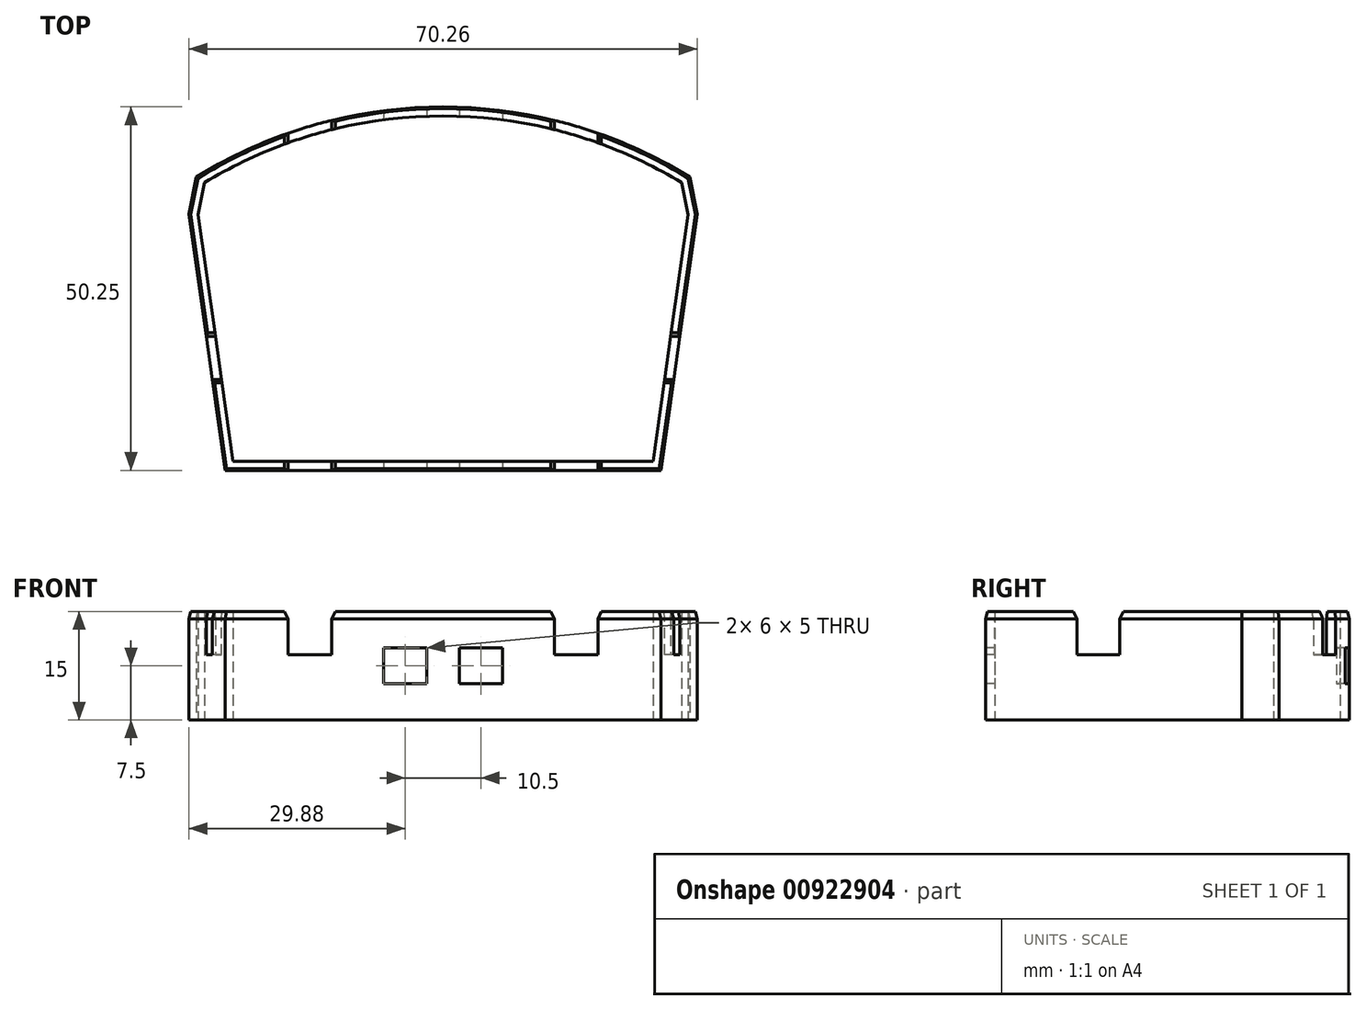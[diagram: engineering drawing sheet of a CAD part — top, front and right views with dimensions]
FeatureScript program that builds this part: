
annotation { "Feature Type Name" : "Feature", "Feature Type Description" : "" }
export const myFeature = defineFeature(function(context is Context, id is Id, definition is map)
    precondition{}
    {
        {
            var Q0;
            Q0=qCreatedBy(makeId("Top.planeOp"),FACE);
            var sketch = newSketch(context, id + "F0", { "sketchPlane" : qUnion([Q0])});
            skLineSegment(sketch, "E0", {"start": v(-30.12, 0) * mm, "end": v(30.12, 0) * mm});
            skLineSegment(sketch, "E1", {"start": v(-30.13, 0) * mm, "end": v(-35.13, 35.4) * mm});
            skLineSegment(sketch, "E2", {"start": v(-35.13, 35.4) * mm, "end": v(-34.13, 40.55) * mm});
            skArc(sketch, "E3", {"start": v(34.12, 40.55) * mm, "mid": v(0, 50.25) * mm, "end": v(-34.12, 40.55) * mm});
            skLineSegment(sketch, "E4", {"start": v(0, 50.25) * mm, "end": v(0, 0) * mm});
            skLineSegment(sketch, "E5.MirrorCS", {"start": v(30.12, 0) * mm, "end": v(35.12, 35.4) * mm});
            skLineSegment(sketch, "E6.MirrorCS", {"start": v(35.13, 35.4) * mm, "end": v(34.13, 40.55) * mm});
            skLineSegment(sketch, "E7.0", {"start": v(33.86, 35.37) * mm, "end": v(33, 39.77) * mm});
            skLineSegment(sketch, "E7.1", {"start": v(-33.86, 35.37) * mm, "end": v(-33, 39.77) * mm});
            skLineSegment(sketch, "E7.2", {"start": v(-29.04, 1.25) * mm, "end": v(-33.86, 35.37) * mm});
            skArc(sketch, "E7.3", {"start": v(33, 39.77) * mm, "mid": v(0, 49) * mm, "end": v(-33, 39.77) * mm});
            skLineSegment(sketch, "E7.4", {"start": v(-29.04, 1.25) * mm, "end": v(29.04, 1.25) * mm});
            skLineSegment(sketch, "E7.5", {"start": v(29.04, 1.25) * mm, "end": v(33.86, 35.37) * mm});
            skSolve(sketch);
        }
        {
            var Q0;
            {var subQ1=sQuery(id+"F0.wireOp",EDGE,"E1");Q0=makeQuery(id+"F0.imprint","IMPRINT",FACE,{"disambiguationData":[TD([[makeQuery(id+"F0.imprint","IMPRINT",EDGE,{"derivedFrom":subQ1}),-1.0]])]});}
            var Q1;
            {var subQ11=sQuery(id+"F0.wireOp",EDGE,"E5.MirrorCS");Q1=makeQuery(id+"F0.imprint","IMPRINT",FACE,{"disambiguationData":[TD([[makeQuery(id+"F0.imprint","IMPRINT",EDGE,{"derivedFrom":subQ11}),1.0]])]});}
            extrude(context, id + "F1", {"entities" : qUnion([Q0, Q1]), "depth" : 12 * mm, "offsetDistance" : 25 * mm});
        }
        {
            var Q0;
            Q0=makeQuery(id+"F1.opExtrude","CAP_EDGE",EDGE,{"disambiguationData":[OSD([sQuery(id+"F0.wireOp",EDGE,"E1")])],"isStart":false});
            var Q1;
            Q1=makeQuery(id+"F1.opExtrude","CAP_EDGE",EDGE,{"disambiguationData":[OSD([sQuery(id+"F0.wireOp",EDGE,"E0")])],"isStart":false});
            var Q2;
            Q2=makeQuery(id+"F1.opExtrude","CAP_EDGE",EDGE,{"disambiguationData":[OSD([sQuery(id+"F0.wireOp",EDGE,"E5.MirrorCS")])],"isStart":false});
            var Q3;
            Q3=makeQuery(id+"F1.opExtrude","CAP_EDGE",EDGE,{"disambiguationData":[OSD([sQuery(id+"F0.wireOp",EDGE,"E3")])],"isStart":false});
            var Q4;
            Q4=makeQuery(id+"F1.opExtrude","CAP_EDGE",EDGE,{"disambiguationData":[OSD([sQuery(id+"F0.wireOp",EDGE,"E6.MirrorCS")])],"isStart":false});
            var Q5;
            Q5=makeQuery(id+"F1.opExtrude","CAP_EDGE",EDGE,{"disambiguationData":[OSD([sQuery(id+"F0.wireOp",EDGE,"E2")])],"isStart":false});
            chamfer(context, id + "F2", {"entities" : qUnion([Q0, Q1, Q2, Q3, Q4, Q5]), "chamferType" : ChamferType.TWO_OFFSETS, "width1" : .25 * mm, "oppositeDirection" : true, "width2" : 1 * mm, "tangentPropagation" : true});
        }
        {
            var Q0;
            Q0=makeQuery(id+"F1.opExtrude","SWEPT_FACE",FACE,{"disambiguationData":[OSD([sQuery(id+"F0.wireOp",EDGE,"E0")])]});
            var sketch = newSketch(context, id + "F3", { "sketchPlane" : qUnion([Q0])});
            skLineSegment(sketch, "E8", {"start": v(-8.25, 2) * mm, "end": v(-2.25, 2) * mm});
            skLineSegment(sketch, "E9", {"start": v(-8.25, 2) * mm, "end": v(-8.25, 7) * mm});
            skLineSegment(sketch, "E10", {"start": v(-2.25, 2) * mm, "end": v(-2.25, 7) * mm});
            skLineSegment(sketch, "E11", {"start": v(-8.25, 7) * mm, "end": v(-2.25, 7) * mm});
            skLineSegment(sketch, "E12.MirrorCS", {"start": v(2.25, 2) * mm, "end": v(2.25, 7) * mm});
            skLineSegment(sketch, "E13.MirrorCS", {"start": v(8.25, 7) * mm, "end": v(2.25, 7) * mm});
            skLineSegment(sketch, "E14.MirrorCS", {"start": v(8.25, 2) * mm, "end": v(8.25, 7) * mm});
            skLineSegment(sketch, "E15.MirrorCS", {"start": v(8.25, 2) * mm, "end": v(2.25, 2) * mm});
            skLineSegment(sketch, "E16.0", {"start": v(-29.9, 12) * mm, "end": v(29.9, 12) * mm, "construction": true});
            skLineSegment(sketch, "E17.0", {"start": v(30.12, 11) * mm, "end": v(-30.12, 11) * mm, "construction": true});
            skLineSegment(sketch, "E18", {"start": v(-21.4, 11) * mm, "end": v(-21.4, 6) * mm});
            skLineSegment(sketch, "E19", {"start": v(-21.4, 6) * mm, "end": v(-15.4, 6) * mm});
            skLineSegment(sketch, "E20", {"start": v(-15.4, 6) * mm, "end": v(-15.4, 11) * mm});
            skLineSegment(sketch, "E21", {"start": v(-21.4, 11) * mm, "end": v(-21.9, 12) * mm});
            skLineSegment(sketch, "E22", {"start": v(-15.4, 11) * mm, "end": v(-14.9, 12) * mm});
            skLineSegment(sketch, "E23", {"start": v(-18.4, 6) * mm, "end": v(-18.4, 12) * mm, "construction": true});
            skLineSegment(sketch, "E24", {"start": v(-21.9, 12) * mm, "end": v(-14.9, 12) * mm});
            skPoint(sketch, "E25", {"position": v(-18.4, 12) * mm});
            skLineSegment(sketch, "E26", {"start": v(-21.4, 11) * mm, "end": v(-15.4, 11) * mm, "construction": true});
            skPoint(sketch, "E27", {"position": v(-18.4, 11) * mm});
            skLineSegment(sketch, "E28.MirrorCS", {"start": v(21.4, 6) * mm, "end": v(15.4, 6) * mm});
            skLineSegment(sketch, "E29.MirrorCS", {"start": v(21.4, 11) * mm, "end": v(21.4, 6) * mm});
            skLineSegment(sketch, "E30.MirrorCS", {"start": v(21.4, 11) * mm, "end": v(21.9, 12) * mm});
            skLineSegment(sketch, "E31.MirrorCS", {"start": v(21.9, 12) * mm, "end": v(14.9, 12) * mm});
            skLineSegment(sketch, "E32.MirrorCS", {"start": v(15.4, 11) * mm, "end": v(14.9, 12) * mm});
            skLineSegment(sketch, "E33.MirrorCS", {"start": v(15.4, 6) * mm, "end": v(15.4, 11) * mm});
            skSolve(sketch);
        }
        {
            var Q0;
            {var subQ0=sQuery(id+"F3.wireOp",EDGE,"E18");Q0=makeQuery(id+"F3.imprint","IMPRINT",FACE,{"disambiguationData":[TD([[makeQuery(id+"F3.imprint","IMPRINT",EDGE,{"derivedFrom":subQ0}),1.0]])]});}
            var Q1;
            {var subQ0=sQuery(id+"F3.wireOp",EDGE,"E21");Q1=makeQuery(id+"F3.imprint","IMPRINT",FACE,{"disambiguationData":[TD([[makeQuery(id+"F3.imprint","IMPRINT",EDGE,{"derivedFrom":subQ0}),-1.0]])]});}
            var Q2;
            Q2=makeQuery(id+"F3.imprint","IMPRINT",FACE,{"disambiguationData":[TD([[makeQuery(id+"F3.imprint","IMPRINT",EDGE,{"derivedFrom":sQuery(id+"F3.wireOp",EDGE,"E28.MirrorCS")}),-1.0]])]});
            var Q3;
            {var subQ0=sQuery(id+"F3.wireOp",EDGE,"E30.MirrorCS");Q3=makeQuery(id+"F3.imprint","IMPRINT",FACE,{"disambiguationData":[TD([[makeQuery(id+"F3.imprint","IMPRINT",EDGE,{"derivedFrom":subQ0}),1.0]])]});}
            var Q4;
            Q4=makeQuery(id+"F3.imprint","IMPRINT",FACE,{"disambiguationData":[TD([[makeQuery(id+"F3.imprint","IMPRINT",EDGE,{"derivedFrom":sQuery(id+"F3.wireOp",EDGE,"E8")}),1.0]])]});
            var Q5;
            Q5=makeQuery(id+"F3.imprint","IMPRINT",FACE,{"disambiguationData":[TD([[makeQuery(id+"F3.imprint","IMPRINT",EDGE,{"derivedFrom":sQuery(id+"F3.wireOp",EDGE,"E12.MirrorCS")}),-1.0]])]});
            extrude(context, id + "F4", {"entities" : qUnion([Q0, Q1, Q2, Q3, Q4, Q5]), "operationType" : NewBodyOperationType.REMOVE, "endBound" : BoundingType.THROUGH_ALL, "oppositeDirection" : true, "depth" : 25 * mm, "offsetDistance" : 25 * mm});
        }
        {
            var Q0;
            Q0=makeQuery(id+"F1.opExtrude","SWEPT_EDGE",EDGE,{"disambiguationData":[OSD([sQuery(id+"F0.wireOp",EDGE,"E1"),sQuery(id+"F0.wireOp",EDGE,"E2")])]});
            cPlane(context, id + "F5", {"entities" : qUnion([Q0]), "cplaneType" : CPlaneType.LINE_ANGLE, "offset" : 25 * mm, "angle" : 0 * degree, "width" : 150 * mm, "height" : 150 * mm});
        }
        {
            var Q0;
            Q0=makeQuery(id+"F1.opExtrude","SWEPT_FACE",FACE,{"disambiguationData":[OSD([sQuery(id+"F0.wireOp",EDGE,"E1")])]});
            var sketch = newSketch(context, id + "F6", { "sketchPlane" : qUnion([Q0])});
            skLineSegment(sketch, "E34.0.0", {"start": v(-4.21, 0) * mm, "end": v(-4.21, 11) * mm});
            skLineSegment(sketch, "E34.0.1", {"start": v(-4.21, 11) * mm, "end": v(-39.96, 11) * mm});
            skLineSegment(sketch, "E34.0.2", {"start": v(-39.96, 11) * mm, "end": v(-39.96, 0) * mm});
            skLineSegment(sketch, "E34.0.3", {"start": v(-39.96, 0) * mm, "end": v(-4.21, 0) * mm});
            skLineSegment(sketch, "E35.0", {"start": v(-39.92, 12) * mm, "end": v(-4.43, 12) * mm});
            skLineSegment(sketch, "E36", {"start": v(-22.93, 11) * mm, "end": v(-22.93, 6) * mm});
            skLineSegment(sketch, "E37", {"start": v(-22.93, 6) * mm, "end": v(-16.93, 6) * mm});
            skLineSegment(sketch, "E38", {"start": v(-16.93, 6) * mm, "end": v(-16.93, 11) * mm});
            skLineSegment(sketch, "E39", {"start": v(-22.93, 11) * mm, "end": v(-23.43, 12) * mm});
            skLineSegment(sketch, "E40", {"start": v(-16.93, 11) * mm, "end": v(-16.43, 12) * mm});
            skLineSegment(sketch, "E41", {"start": v(-19.93, 6) * mm, "end": v(-19.93, 12) * mm, "construction": true});
            skLineSegment(sketch, "E42", {"start": v(-23.43, 12) * mm, "end": v(-16.43, 12) * mm});
            skPoint(sketch, "E43", {"position": v(-19.93, 12) * mm});
            skLineSegment(sketch, "E44", {"start": v(-22.93, 11) * mm, "end": v(-16.93, 11) * mm, "construction": true});
            skPoint(sketch, "E45", {"position": v(-19.93, 11) * mm});
            skSolve(sketch);
        }
        {
            var Q0;
            Q0=qCreatedBy(id+"F5.planeOp",FACE);
            var sketch = newSketch(context, id + "F7", { "sketchPlane" : qUnion([Q0])});
            skLineSegment(sketch, "E46.0", {"start": v(-18.53, 11) * mm, "end": v(-18.53, 6) * mm});
            skLineSegment(sketch, "E47.0", {"start": v(-18.53, 11) * mm, "end": v(-19.03, 12) * mm});
            skLineSegment(sketch, "E48.0", {"start": v(-19.03, 12) * mm, "end": v(-12.1, 12) * mm});
            skLineSegment(sketch, "E49.0", {"start": v(-12.6, 11) * mm, "end": v(-12.1, 12) * mm});
            skLineSegment(sketch, "E50.0", {"start": v(-12.6, 6) * mm, "end": v(-12.6, 11) * mm});
            skLineSegment(sketch, "E51.0", {"start": v(-18.53, 6) * mm, "end": v(-12.6, 6) * mm});
            skSolve(sketch);
        }
        {
            var Q0;
            Q0=makeQuery(id+"F7.imprint","IMPRINT",FACE,{"disambiguationData":[TD([[makeQuery(id+"F7.imprint","IMPRINT",EDGE,{"derivedFrom":sQuery(id+"F7.wireOp",EDGE,"E46.0")}),1.0]])]});
            extrude(context, id + "F8", {"entities" : qUnion([Q0]), "operationType" : NewBodyOperationType.REMOVE, "endBound" : BoundingType.THROUGH_ALL, "oppositeDirection" : true, "depth" : 25 * mm, "offsetDistance" : 25 * mm});
        }
        {
            var Q0;
            {var subQ0=sQuery(id+"F0.wireOp",EDGE,"E2");var subQ1=sQuery(id+"F0.wireOp",EDGE,"E1");var subQ2=sQuery(id+"F0.wireOp",EDGE,"E3");var subQ3=sQuery(id+"F0.wireOp",EDGE,"E0");var subQ4=sQuery(id+"F0.wireOp",EDGE,"E7.3");var subQ5=sQuery(id+"F0.wireOp",EDGE,"E7.1");var subQ6=sQuery(id+"F0.wireOp",EDGE,"E7.2");var subQ7=sQuery(id+"F0.wireOp",EDGE,"E7.4");Q0=makeQuery(id+"F4.boolean.opBoolean","SPLIT",FACE,{"disambiguationData":[TD([makeQuery(id+"F1.opExtrude","SWEPT_FACE",FACE,{"disambiguationData":[OSD([subQ3])]}),makeQuery(id+"F1.opExtrude","SWEPT_FACE",FACE,{"disambiguationData":[OSD([subQ1])]}),makeQuery(id+"F1.opExtrude","SWEPT_FACE",FACE,{"disambiguationData":[OSD([subQ0])]}),makeQuery(id+"F1.opExtrude","SWEPT_FACE",FACE,{"disambiguationData":[OSD([subQ2])]}),makeQuery(id+"F1.opExtrude","SWEPT_FACE",FACE,{"disambiguationData":[OSD([subQ5])]}),makeQuery(id+"F1.opExtrude","SWEPT_FACE",FACE,{"disambiguationData":[OSD([subQ6])]}),makeQuery(id+"F1.opExtrude","SWEPT_FACE",FACE,{"disambiguationData":[OSD([subQ4])]}),makeQuery(id+"F1.opExtrude","SWEPT_FACE",FACE,{"disambiguationData":[OSD([subQ7])]}),makeQuery(id+"F4.opExtrude","SWEPT_FACE",FACE,{"disambiguationData":[OSD([sQuery(id+"F3.wireOp",EDGE,"E9")])]})])],"derivedFrom":makeQuery(id+"F1.opExtrude","CAP_FACE",FACE,{"disambiguationData":[OSD([subQ3,subQ1,subQ0,subQ2,sQuery(id+"F0.wireOp",EDGE,"E5.MirrorCS"),sQuery(id+"F0.wireOp",EDGE,"E6.MirrorCS"),sQuery(id+"F0.wireOp",EDGE,"E7.0"),subQ5,subQ6,subQ4,subQ7,sQuery(id+"F0.wireOp",EDGE,"E7.5")])],"isStart":true})});}
            var sketch = newSketch(context, id + "F9", { "sketchPlane" : qUnion([Q0])});
            skLineSegment(sketch, "E52.0", {"start": v(-30.12, 0) * mm, "end": v(30.12, 0) * mm});
            skLineSegment(sketch, "E53.0", {"start": v(-35.13, -35.4) * mm, "end": v(-30.13, 0) * mm});
            skLineSegment(sketch, "E54.0", {"start": v(-35.13, -35.4) * mm, "end": v(-34.13, -40.55) * mm});
            skArc(sketch, "E55.0", {"start": v(34.12, -40.55) * mm, "mid": v(0, -50.25) * mm, "end": v(-34.12, -40.55) * mm});
            skLineSegment(sketch, "E56.0", {"start": v(35.13, -35.4) * mm, "end": v(34.13, -40.55) * mm});
            skLineSegment(sketch, "E57.0", {"start": v(30.12, 0) * mm, "end": v(35.12, -35.4) * mm});
            skLineSegment(sketch, "E58.0", {"start": v(-29.04, -1.25) * mm, "end": v(29.04, -1.25) * mm});
            skLineSegment(sketch, "E59.0", {"start": v(-29.04, -1.25) * mm, "end": v(-33.86, -35.37) * mm});
            skLineSegment(sketch, "E60.0", {"start": v(-33.86, -35.37) * mm, "end": v(-33, -39.77) * mm});
            skArc(sketch, "E61.0", {"start": v(33, -39.77) * mm, "mid": v(0, -49) * mm, "end": v(-33, -39.77) * mm});
            skLineSegment(sketch, "E62.0", {"start": v(33.86, -35.37) * mm, "end": v(33, -39.77) * mm});
            skLineSegment(sketch, "E63.0", {"start": v(29.04, -1.25) * mm, "end": v(33.86, -35.37) * mm});
            skSolve(sketch);
        }
        {
            var Q0;
            {var subQ1=sQuery(id+"F9.wireOp",EDGE,"E53.0");Q0=makeQuery(id+"F9.imprint","IMPRINT",FACE,{"disambiguationData":[TD([[makeQuery(id+"F9.imprint","IMPRINT",EDGE,{"derivedFrom":subQ1}),1.0]])]});}
            var Q1;
            {var subQ1=sQuery(id+"F0.wireOp",EDGE,"E1");Q1=makeQuery(id+"F0.imprint","IMPRINT",FACE,{"disambiguationData":[TD([[makeQuery(id+"F0.imprint","IMPRINT",EDGE,{"derivedFrom":subQ1}),-1.0]])]});}
            var Q2;
            {var subQ11=sQuery(id+"F0.wireOp",EDGE,"E5.MirrorCS");Q2=makeQuery(id+"F0.imprint","IMPRINT",FACE,{"disambiguationData":[TD([[makeQuery(id+"F0.imprint","IMPRINT",EDGE,{"derivedFrom":subQ11}),1.0]])]});}
            extrude(context, id + "F10", {"entities" : qUnion([Q0, Q1, Q2]), "operationType" : NewBodyOperationType.ADD, "depth" : 3 * mm, "offsetDistance" : 25 * mm});
        }
    });
